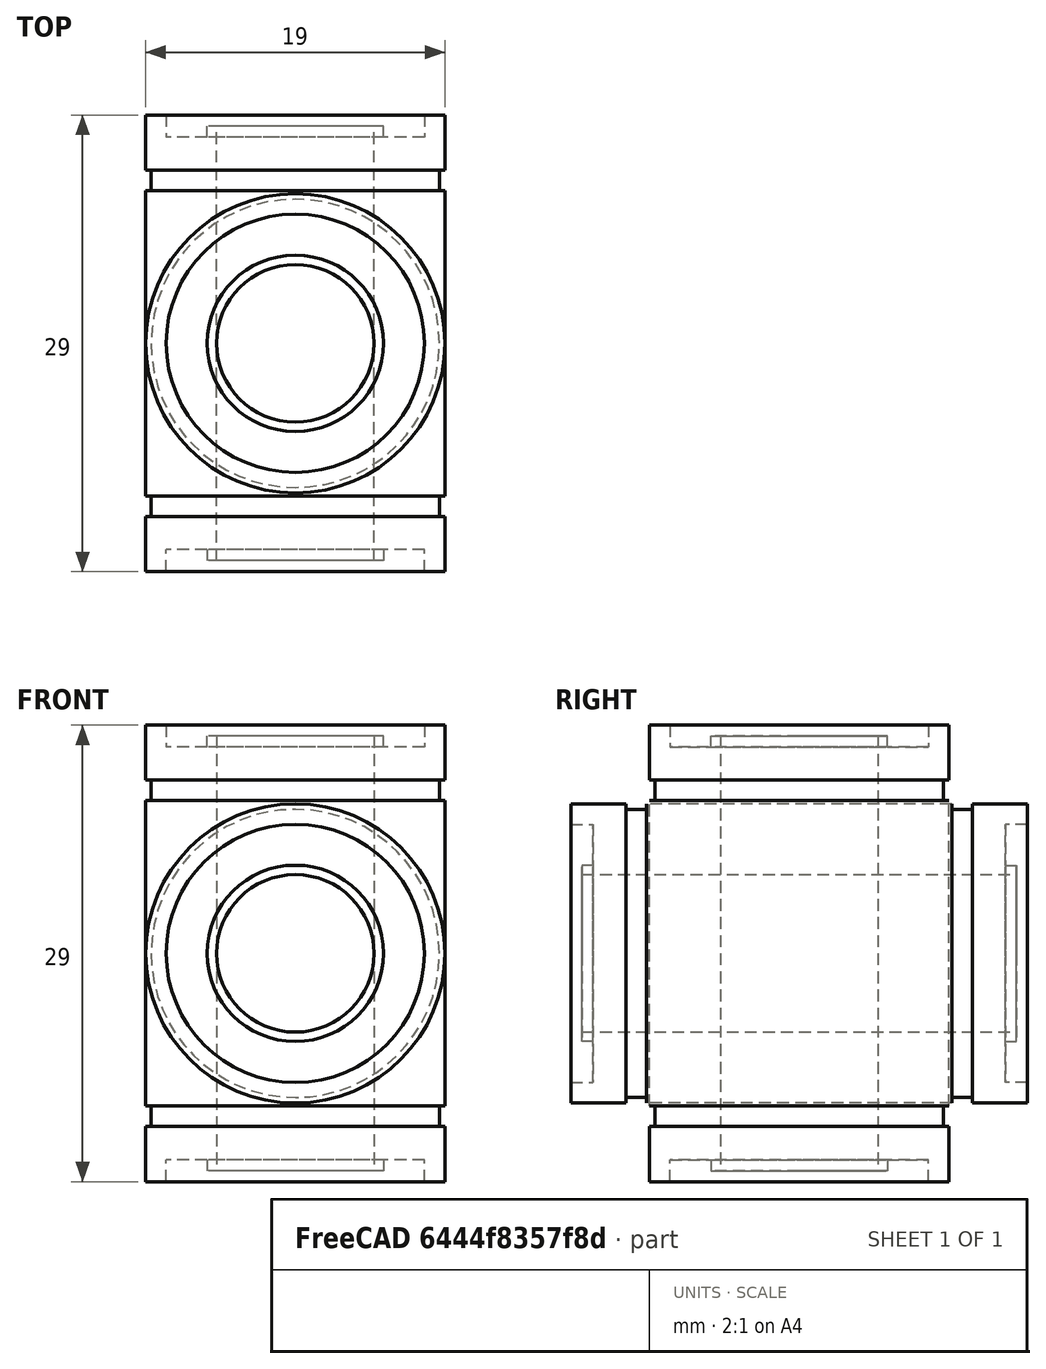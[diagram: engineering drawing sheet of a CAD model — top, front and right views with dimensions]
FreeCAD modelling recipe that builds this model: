
FCSTD DOCUMENT  (FreeCAD 0.15R4630 (Git))
Label: LM10uu
Comment: Modified LM8UU to LM10UU specs
License: CC-BY 3.0
LicenseURL: http://creativecommons.org/licenses/by/3.0/
objects: Sketcher::SketchObject×1, PartDesign::Revolution×1, Part::Feature×1
note: 4 computed .brp shape members not serialized (recipe doc carries the construction recipe); baked Part::Feature solids carry a one-line shape summary decoded from their .brp

FEATURE [Sketcher::SketchObject] Sketch  label="lm10uu-cross-section"
  Placement = pos=(0,0,0) rot=(1,0,0;1.5708rad)
  sketch-geometry (20):
    g0: LineSegment StartX=9.5 StartY=-14.5 StartZ=0 EndX=9.5 EndY=-11 EndZ=0
    g1: LineSegment StartX=9.5 StartY=9.7 StartZ=0 EndX=9.15 EndY=9.7 EndZ=0
    g2: LineSegment StartX=9.15 StartY=9.7 StartZ=0 EndX=9.15 EndY=11 EndZ=0
    g3: LineSegment StartX=9.15 StartY=11 StartZ=0 EndX=9.5 EndY=11 EndZ=0
    g4: LineSegment StartX=9.5 StartY=11 StartZ=0 EndX=9.5 EndY=14.5 EndZ=0
    g5: LineSegment StartX=9.5 StartY=14.5 StartZ=0 EndX=8.2 EndY=14.5 EndZ=0
    g6: LineSegment StartX=8.2 StartY=14.5 StartZ=0 EndX=8.2 EndY=13.1 EndZ=0
    g7: LineSegment StartX=8.2 StartY=13.1 StartZ=0 EndX=5.6 EndY=13.1 EndZ=0
    g8: LineSegment StartX=5.6 StartY=13.1 StartZ=0 EndX=5.6 EndY=13.8 EndZ=0
    g9: LineSegment StartX=5.6 StartY=13.8 StartZ=0 EndX=5 EndY=13.8 EndZ=0
    g10: LineSegment StartX=5 StartY=13.8 StartZ=0 EndX=5 EndY=-13.8 EndZ=0
    g11: LineSegment StartX=9.5 StartY=-9.7 StartZ=0 EndX=9.15 EndY=-9.7 EndZ=0
    g12: LineSegment StartX=9.15 StartY=-11 StartZ=0 EndX=9.5 EndY=-11 EndZ=0
    g13: LineSegment StartX=9.5 StartY=-9.7 StartZ=0 EndX=9.5 EndY=9.7 EndZ=0
    g14: LineSegment StartX=9.15 StartY=-9.7 StartZ=0 EndX=9.15 EndY=-11 EndZ=0
    g15: LineSegment StartX=9.5 StartY=-14.5 StartZ=0 EndX=8.2 EndY=-14.5 EndZ=0
    g16: LineSegment StartX=8.2 StartY=-14.5 StartZ=0 EndX=8.2 EndY=-13.1 EndZ=0
    g17: LineSegment StartX=8.2 StartY=-13.1 StartZ=0 EndX=5.6 EndY=-13.1 EndZ=0
    g18: LineSegment StartX=5.6 StartY=-13.1 StartZ=0 EndX=5.6 EndY=-13.8 EndZ=0
    g19: LineSegment StartX=5.6 StartY=-13.8 StartZ=0 EndX=5 EndY=-13.8 EndZ=0
  constraints (58):
    c: Coincident(g13,g1)
    c: Coincident(g1,g2)
    c: Vertical(g2)
    c: Coincident(g2,g3)
    c: Coincident(g3,g4)
    c: Vertical(g4)
    c: Coincident(g4,g5)
    c: Coincident(g5,g6)
    c: Vertical(g6)
    c: Coincident(g6,g7)
    c: Horizontal(g7)
    c: Coincident(g7,g8)
    c: Vertical(g8)
    c: Coincident(g8,g9)
    c: Horizontal(g9)
    c: Coincident(g9,g10)
    c: Vertical(g10)
    c: Horizontal(g1)
    c: Horizontal(g5)
    c: Horizontal(g3)
    c: PointOnObject(g3,g0)
    c: Symmetric(g0,g4,g-1)
    c: DistanceY(g4,g0) = -29
    c: DistanceY(g2) = 1.3
    c: DistanceX(g3) = 0.35
    c: DistanceX(g-1,g4) = 9.5
    c: DistanceX(g-1,g9) = 5
    c: DistanceX(g5) = -1.3
    c: DistanceX(g9) = -0.6
    c: DistanceY(g6) = -1.4
    c: DistanceY(g8) = 0.7
    c: Horizontal(g11)
    c: Horizontal(g12)
    c: Coincident(g13,g11)
    c: Tangent(g0,g13)
    c: Coincident(g12,g0)
    c: PointOnObject(g14,g11)
    c: Coincident(g14,g12)
    c: Vertical(g14)
    c: Symmetric(g1,g11,g-1)
    c: DistanceY(g13) = 19.4
    c: Equal(g14,g2)
    c: Coincident(g0,g15)
    c: Horizontal(g15)
    c: Coincident(g15,g16)
    c: Vertical(g16)
    c: Coincident(g16,g17)
    c: Horizontal(g17)
    c: Coincident(g17,g18)
    c: Vertical(g18)
    c: Coincident(g18,g19)
    c: Horizontal(g19)
    c: Coincident(g10,g19)
    c: Symmetric(g10,g9,g-1)
    c: Symmetric(g16,g6,g-1)
    c: Symmetric(g17,g7,g-1)
    c: Coincident(g14,g11)
    c: PointOnObject(g11,g2)
FEATURE [PartDesign::Revolution] Revolution  label="LM10uu"
  Angle = 360
  Axis = (0,0,1)
  Base = (0,0,0)
  Placement = pos=(0,0,0) rot=(1,0,0;1.5708rad)
  ReferenceAxis = -> Sketch [V_Axis]
  Reversed = true
  Sketch = -> Sketch
FEATURE [Part::Feature] Revolution001  label="LM10uu001"
  Placement = pos=(0,0,0) rot=(1,0,0;1.5708rad)
  shape: bbox 19 x 29 x 19 mm, 20 faces (baked)
